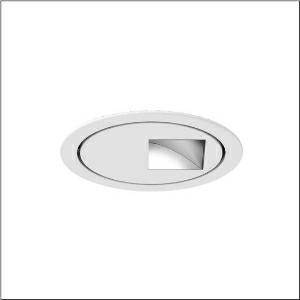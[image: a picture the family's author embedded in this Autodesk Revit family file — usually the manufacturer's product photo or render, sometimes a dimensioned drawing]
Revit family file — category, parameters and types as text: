
# Revit family: lunis_11_mini_round_51dk11b72wn21
name_source: partatom
category: Lighting Fixtures
units: mm (PartAtom-declared; Revit-internal decimal feet)

## family parameters
Cut with Voids When Loaded = No
Host = Face
Light Source = No
Part Type = Normal
Room Calculation Point = No
Round Connector Dimension = Use Diameter
Shared = No

## types (1)
- Lunis 11 mini round (1 x LED 4000K / CRI = 90 (unbekannt), 2120 lm, 4000K)
    Apparent Load = 28 VA
    CIE Flux Codes = 44 77 97 100 100
    Color Rendering = 90
    Color Temperature = 4000K
    Default Elevation = 1800 mm
    Description = Lunis 11 mini round, downlight, light control with wallwasher, of highly reflective aluminium, highly specular, light emission: direct distribution, LED rated luminous flux: 2.120lm, light colour: 940, control gear: ECG, with terminal, 3-pole, mains connection: 220..230V, AC/DC, 0/50..60Hz, LED module, luminaire module, of aluminium, highly specular, white, diameter: 176mm, clamping range: 1..40mm, recessing ring, of plastic, traffic white (RAL 9016), protection rating (complete): IP20, insulation class (complete): insulation class II (safety insulation), certification: CE, permissible ambient temperature for indoor applications: 0..+35°C, packaging unit: 1 piece
    Height = 0 mm  [stored 0 ft]
    Lamp = 1 x LED 4000K / CRI >= 90 (unbekannt)
    Lamp Light Flux = 2120 lm
    Lamp count = 1
    Length = 176 mm
    Luminous efficacy = 75 lm/W
    Manufacturer = Siteco
    ModVariant = No
    Model = 51DK11B72WN21
    Mounting Place = Ceiling
    Mounting Type = Recessed
    Number of Poles = 1
    OnlyDefault = Yes
    Power Factor = 1
    Product Name = Lunis 11 mini round
    Product group = downlight
    ProductGroupID = 401
    Protection Class = Protection class II
    Protection Degree = IP 20
    RLX_Detail_Level = 1
    RLX_Emergency_Light_Flux = 0 lm
    RLX_Emergency_Type = 0
    RLX_Emergency_Type_DB = No
    RlxData = <blob elided: 59281 chars, md5=5e05c846>
    Socket = socket
    Standby Power = 0 W
    System Light Flux = 2120 lm
    System Power = 28 W
    Type Comments = Product without accessories
    Type Image = l_1004772.jpg
    URL = http://relux.com
    VarID = ---
    Voltage = 0 V
    Weight = 0.00 kg
    Width = 176 mm

note: [stored X ft] marks values corroborated as IEEE doubles in the binary element streams (Revit-internal decimal feet)

## geometry (parser evidence)
native form markers: Blend x4, Sweep x10
no freeform markers — native parametric forms only
